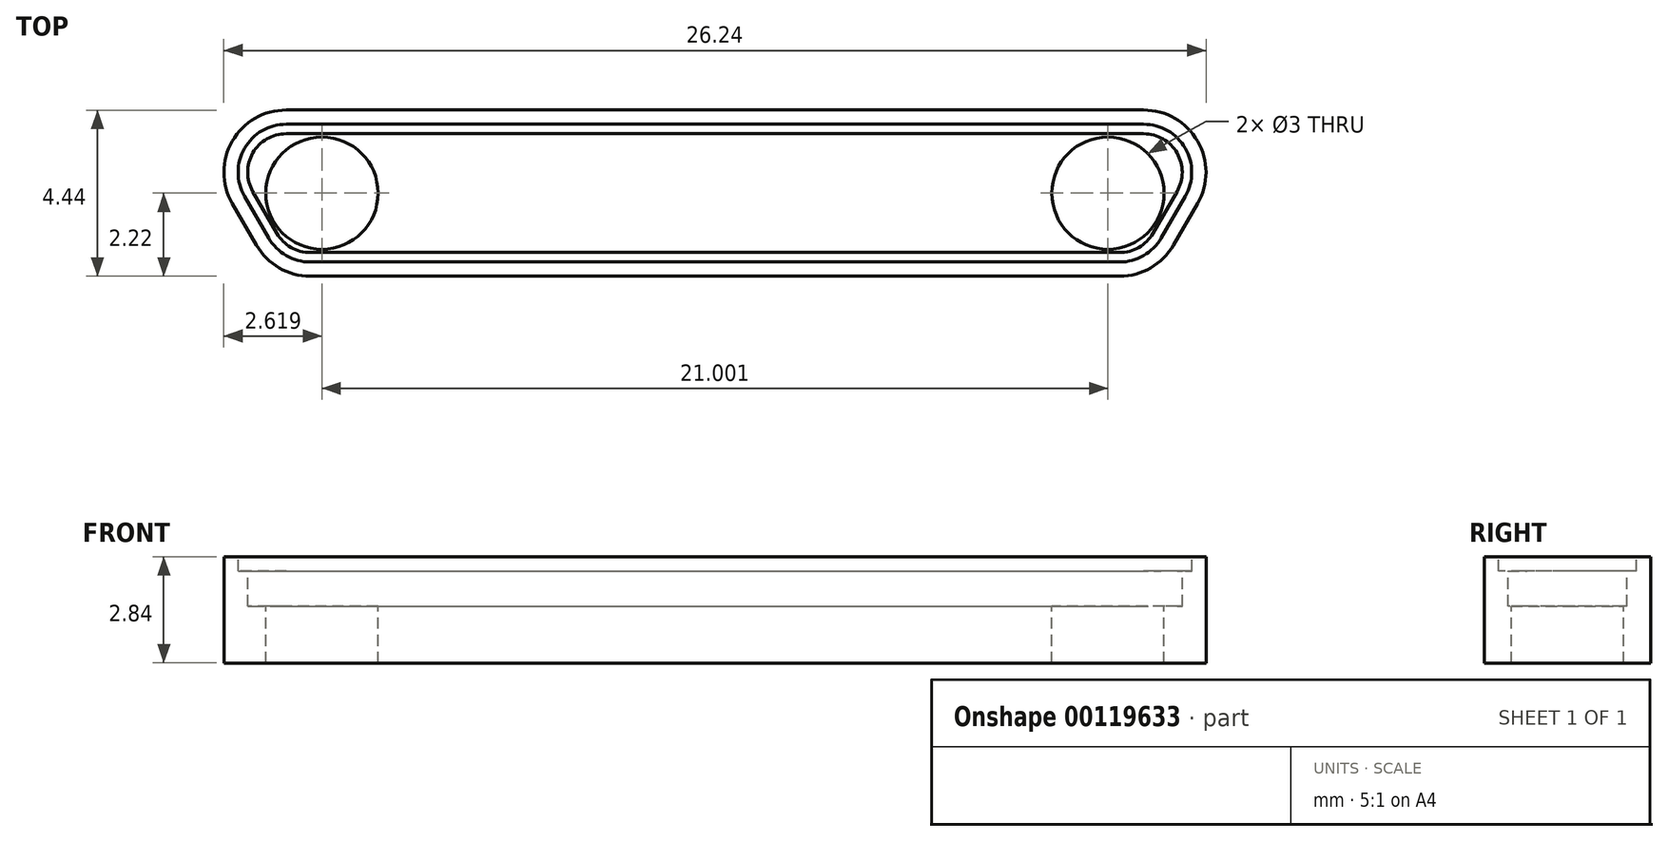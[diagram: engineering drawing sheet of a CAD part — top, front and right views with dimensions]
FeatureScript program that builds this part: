
annotation { "Feature Type Name" : "Feature", "Feature Type Description" : "" }
export const myFeature = defineFeature(function(context is Context, id is Id, definition is map)
    precondition{}
    {
        {
            var Q0;
            Q0=qCreatedBy(makeId("Top.planeOp"),FACE);
            var sketch = newSketch(context, id + "F0", { "sketchPlane" : qUnion([Q0])});
            skLineSegment(sketch, "E0.bottom", {"start": v(-11.46, 2.22) * mm, "end": v(11.46, 2.22) * mm});
            skLineSegment(sketch, "E0.top", {"start": v(-10.81, -2.22) * mm, "end": v(10.81, -2.22) * mm});
            skLineSegment(sketch, "E0.left", {"start": v(-12.9, -0.27) * mm, "end": v(-12.25, -1.4) * mm});
            skLineSegment(sketch, "E0.right", {"start": v(12.9, -0.27) * mm, "end": v(12.25, -1.4) * mm});
            skPoint(sketch, "E0.middle", {"position": v(0, 0) * mm});
            skArc(sketch, "E1.filletArc", {"start": v(-11.46, 2.22) * mm, "mid": v(-12.9, 1.4) * mm, "end": v(-12.9, -0.27) * mm});
            skArc(sketch, "E2.filletArc", {"start": v(12.9, -0.27) * mm, "mid": v(12.9, 1.4) * mm, "end": v(11.46, 2.22) * mm});
            skArc(sketch, "E3.filletArc", {"start": v(10.81, -2.22) * mm, "mid": v(11.64, -2) * mm, "end": v(12.25, -1.4) * mm});
            skArc(sketch, "E4.filletArc", {"start": v(-12.25, -1.4) * mm, "mid": v(-11.64, -2) * mm, "end": v(-10.81, -2.22) * mm});
            skLineSegment(sketch, "E5", {"start": v(17.89, 0) * mm, "end": v(-18.73, 0) * mm, "construction": true});
            skLineSegment(sketch, "E6", {"start": v(0, 7.95) * mm, "end": v(0, -9.87) * mm, "construction": true});
            skArc(sketch, "E7.0", {"start": v(-11.46, 1.84) * mm, "mid": v(-12.57, 1.2) * mm, "end": v(-12.57, -0.08) * mm});
            skLineSegment(sketch, "E7.1", {"start": v(-12.57, -0.08) * mm, "end": v(-11.92, -1.2) * mm});
            skLineSegment(sketch, "E7.2", {"start": v(-11.46, 1.84) * mm, "end": v(11.46, 1.84) * mm});
            skArc(sketch, "E7.3", {"start": v(-11.92, -1.2) * mm, "mid": v(-11.45, -1.67) * mm, "end": v(-10.81, -1.84) * mm});
            skArc(sketch, "E7.4", {"start": v(12.57, -0.08) * mm, "mid": v(12.57, 1.2) * mm, "end": v(11.46, 1.84) * mm});
            skLineSegment(sketch, "E7.5", {"start": v(12.57, -0.08) * mm, "end": v(11.92, -1.2) * mm});
            skArc(sketch, "E7.6", {"start": v(10.81, -1.84) * mm, "mid": v(11.45, -1.67) * mm, "end": v(11.92, -1.2) * mm});
            skLineSegment(sketch, "E7.7", {"start": v(-10.81, -1.84) * mm, "end": v(10.81, -1.84) * mm});
            skArc(sketch, "E8.0", {"start": v(-11.46, 1.59) * mm, "mid": v(-12.35, 1.07) * mm, "end": v(-12.35, 0.04) * mm});
            skLineSegment(sketch, "E8.1", {"start": v(-12.35, 0.04) * mm, "end": v(-11.7, -1.07) * mm});
            skLineSegment(sketch, "E8.2", {"start": v(-11.46, 1.59) * mm, "end": v(11.46, 1.59) * mm});
            skArc(sketch, "E8.3", {"start": v(-11.7, -1.07) * mm, "mid": v(-11.32, -1.45) * mm, "end": v(-10.81, -1.59) * mm});
            skArc(sketch, "E8.4", {"start": v(12.35, 0.04) * mm, "mid": v(12.35, 1.07) * mm, "end": v(11.46, 1.59) * mm});
            skLineSegment(sketch, "E8.5", {"start": v(12.35, 0.04) * mm, "end": v(11.7, -1.07) * mm});
            skArc(sketch, "E8.6", {"start": v(10.81, -1.59) * mm, "mid": v(11.32, -1.45) * mm, "end": v(11.7, -1.07) * mm});
            skLineSegment(sketch, "E8.7", {"start": v(-10.81, -1.59) * mm, "end": v(10.81, -1.59) * mm});
            skCircle(sketch, "E9", {"center": v(-10.5, 0) * mm, "radius": 1.5 * mm});
            skCircle(sketch, "E10", {"center": v(10.5, 0) * mm, "radius": 1.5 * mm});
            skLineSegment(sketch, "E11.0", {"start": v(-12.33, 0.17) * mm, "end": v(-11.71, -0.9) * mm, "construction": true});
            skLineSegment(sketch, "E12.0", {"start": v(12.35, 0.2) * mm, "end": v(11.74, -0.86) * mm, "construction": true});
            skSolve(sketch);
        }
        {
            var Q0;
            Q0=makeQuery(id+"F0.imprint","IMPRINT",FACE,{"disambiguationData":[TD([[makeQuery(id+"F0.imprint","IMPRINT",EDGE,{"derivedFrom":sQuery(id+"F0.wireOp",EDGE,"E0.bottom")}),-1.0]])]});
            var Q1;
            Q1=makeQuery(id+"F0.imprint","IMPRINT",FACE,{"disambiguationData":[TD([[makeQuery(id+"F0.imprint","IMPRINT",EDGE,{"derivedFrom":sQuery(id+"F0.wireOp",EDGE,"E7.0")}),1.0]])]});
            var Q2;
            Q2=makeQuery(id+"F0.imprint","IMPRINT",FACE,{"disambiguationData":[TD([[makeQuery(id+"F0.imprint","IMPRINT",EDGE,{"derivedFrom":sQuery(id+"F0.wireOp",EDGE,"E8.0")}),1.0]])]});
            var Q3;
            Q3=makeQuery(id+"F0.imprint","IMPRINT",FACE,{"disambiguationData":[TD([[makeQuery(id+"F0.imprint","IMPRINT",EDGE,{"derivedFrom":sQuery(id+"F0.wireOp",EDGE,"E9")}),1.0]])]});
            var Q4;
            Q4=makeQuery(id+"F0.imprint","IMPRINT",FACE,{"disambiguationData":[TD([[makeQuery(id+"F0.imprint","IMPRINT",EDGE,{"derivedFrom":sQuery(id+"F0.wireOp",EDGE,"E10")}),1.0]])]});
            extrude(context, id + "F1", {"entities" : qUnion([Q0, Q1, Q2, Q3, Q4]), "oppositeDirection" : true, "depth" : 2.84 * mm});
        }
        {
            var Q0;
            Q0=makeQuery(id+"F0.imprint","IMPRINT",FACE,{"disambiguationData":[TD([[makeQuery(id+"F0.imprint","IMPRINT",EDGE,{"derivedFrom":sQuery(id+"F0.wireOp",EDGE,"E8.0")}),1.0]])]});
            var Q1;
            Q1=makeQuery(id+"F0.imprint","IMPRINT",FACE,{"disambiguationData":[TD([[makeQuery(id+"F0.imprint","IMPRINT",EDGE,{"derivedFrom":sQuery(id+"F0.wireOp",EDGE,"E9")}),1.0]])]});
            var Q2;
            Q2=makeQuery(id+"F0.imprint","IMPRINT",FACE,{"disambiguationData":[TD([[makeQuery(id+"F0.imprint","IMPRINT",EDGE,{"derivedFrom":sQuery(id+"F0.wireOp",EDGE,"E10")}),1.0]])]});
            extrude(context, id + "F2", {"entities" : qUnion([Q0, Q1, Q2]), "operationType" : NewBodyOperationType.REMOVE, "oppositeDirection" : true, "depth" : 1.32 * mm});
        }
        {
            var Q0;
            Q0=makeQuery(id+"F0.imprint","IMPRINT",FACE,{"disambiguationData":[TD([[makeQuery(id+"F0.imprint","IMPRINT",EDGE,{"derivedFrom":sQuery(id+"F0.wireOp",EDGE,"E7.0")}),1.0]])]});
            extrude(context, id + "F3", {"entities" : qUnion([Q0]), "operationType" : NewBodyOperationType.REMOVE, "oppositeDirection" : true, "depth" : 0.38 * mm});
        }
        {
            var Q0;
            Q0=makeQuery(id+"F0.imprint","IMPRINT",FACE,{"disambiguationData":[TD([[makeQuery(id+"F0.imprint","IMPRINT",EDGE,{"derivedFrom":sQuery(id+"F0.wireOp",EDGE,"E9")}),1.0]])]});
            var Q1;
            Q1=makeQuery(id+"F0.imprint","IMPRINT",FACE,{"disambiguationData":[TD([[makeQuery(id+"F0.imprint","IMPRINT",EDGE,{"derivedFrom":sQuery(id+"F0.wireOp",EDGE,"E10")}),1.0]])]});
            extrude(context, id + "F4", {"entities" : qUnion([Q0, Q1]), "operationType" : NewBodyOperationType.REMOVE, "endBound" : BoundingType.THROUGH_ALL, "oppositeDirection" : true, "depth" : 25.4 * mm});
        }
    });
